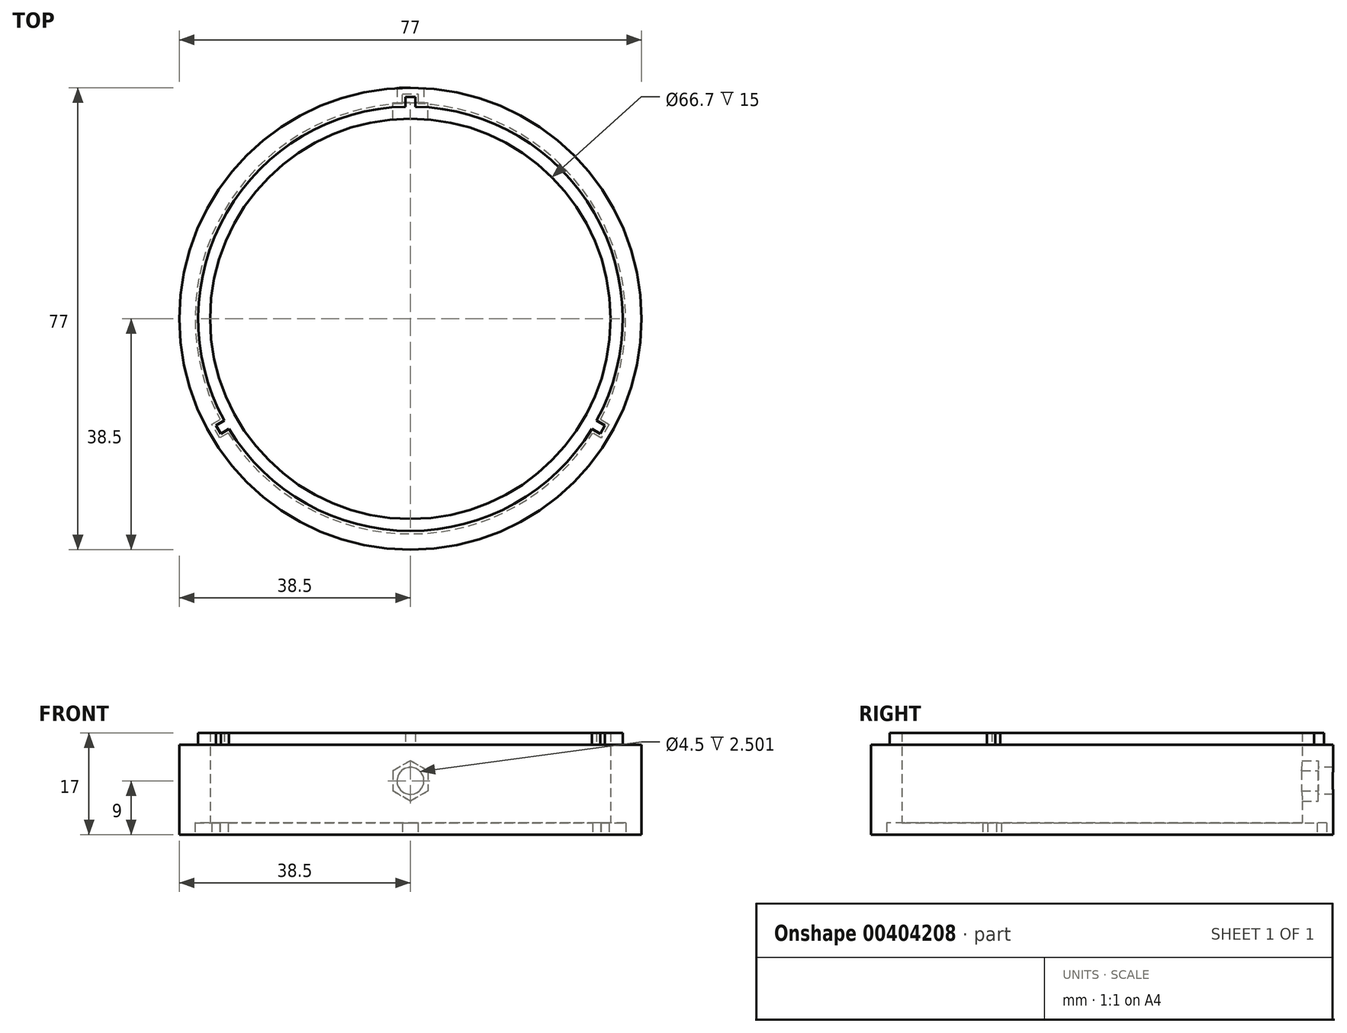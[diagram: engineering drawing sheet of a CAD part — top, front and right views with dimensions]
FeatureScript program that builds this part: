
annotation { "Feature Type Name" : "Feature", "Feature Type Description" : "" }
export const myFeature = defineFeature(function(context is Context, id is Id, definition is map)
    precondition{}
    {
        {
            var Q0;
            Q0=qCreatedBy(makeId("Top.planeOp"),FACE);
            var sketch = newSketch(context, id + "F0", { "sketchPlane" : qUnion([Q0])});
            skCircle(sketch, "E0", {"center": v(0, 0) * mm, "radius": 33.35 * mm});
            skCircle(sketch, "E1", {"center": v(0, 0) * mm, "radius": 38.5 * mm});
            skSolve(sketch);
        }
        {
            var Q0;
            Q0=qSketchRegion(id+"F0",true);
            extrude(context, id + "F1", {"entities" : qUnion([Q0]), "depth" : 15 * mm});
        }
        {
            var Q0;
            Q0=qCreatedBy(makeId("Front.planeOp"),FACE);
            var sketch = newSketch(context, id + "F2", { "sketchPlane" : qUnion([Q0])});
            skCircle(sketch, "E2", {"center": v(0, 9) * mm, "radius": 2.25 * mm});
            skSolve(sketch);
        }
        {
            var Q0;
            Q0=qSketchRegion(id+"F2",true);
            extrude(context, id + "F3", {"entities" : qUnion([Q0]), "operationType" : NewBodyOperationType.REMOVE, "endBound" : BoundingType.THROUGH_ALL, "oppositeDirection" : true, "depth" : 25 * mm});
        }
        {
            var Q0;
            Q0=qCreatedBy(makeId("Front.planeOp"),FACE);
            cPlane(context, id + "F4", {"entities" : qUnion([Q0]), "cplaneType" : CPlaneType.OFFSET, "offset" : 36 * mm, "oppositeDirection" : true, "width" : 150 * mm, "height" : 150 * mm});
        }
        {
            var Q0;
            Q0=qCreatedBy(id+"F4.planeOp",FACE);
            var sketch = newSketch(context, id + "F5", { "sketchPlane" : qUnion([Q0])});
            skCircle(sketch, "E3.cCircle", {"center": v(0, 9) * mm, "radius": 2.92 * mm, "construction": true});
            skLineSegment(sketch, "E3.0", {"start": v(2.92, 10.68) * mm, "end": v(2.92, 7.32) * mm});
            skLineSegment(sketch, "E3.1", {"start": v(2.92, 7.32) * mm, "end": v(0, 5.63) * mm});
            skLineSegment(sketch, "E3.2", {"start": v(0, 5.63) * mm, "end": v(-2.92, 7.32) * mm});
            skLineSegment(sketch, "E3.3", {"start": v(-2.92, 7.32) * mm, "end": v(-2.92, 10.68) * mm});
            skLineSegment(sketch, "E3.4", {"start": v(-2.92, 10.68) * mm, "end": v(0, 12.37) * mm});
            skLineSegment(sketch, "E3.5", {"start": v(0, 12.37) * mm, "end": v(2.92, 10.68) * mm});
            skPoint(sketch, "E3.0.midPoint", {"position": v(2.92, 9) * mm});
            skSolve(sketch);
        }
        {
            var Q0;
            Q0=qSketchRegion(id+"F5",true);
            extrude(context, id + "F6", {"entities" : qUnion([Q0]), "operationType" : NewBodyOperationType.REMOVE, "depth" : 4 * mm});
        }
        {
            var Q0;
            Q0=makeQuery(id+"F1.opExtrude","CAP_FACE",FACE,{"disambiguationData":[OSD([sQuery(id+"F0.wireOp",EDGE,"E0"),sQuery(id+"F0.wireOp",EDGE,"E1")])],"isStart":false});
            var sketch = newSketch(context, id + "F7", { "sketchPlane" : qUnion([Q0])});
            skCircle(sketch, "E4", {"center": v(0, 0) * mm, "radius": 33.35 * mm});
            skArc(sketch, "E5", {"start": v(-0.8, 35.34) * mm, "mid": v(-30.61, 17.68) * mm, "end": v(-31, -16.98) * mm});
            skLineSegment(sketch, "E6", {"start": v(-0.8, 35.34) * mm, "end": v(-0.8, 36.94) * mm});
            skLineSegment(sketch, "E7.MirrorCS", {"start": v(0.8, 35.34) * mm, "end": v(0.8, 36.94) * mm});
            skLineSegment(sketch, "E8", {"start": v(-0.8, 36.94) * mm, "end": v(0.8, 36.94) * mm});
            skLineSegment(sketch, "E9.1.0", {"start": v(-30.2, -18.36) * mm, "end": v(-31.6, -19.16) * mm});
            skLineSegment(sketch, "E9.1.1", {"start": v(-31.6, -19.16) * mm, "end": v(-32.4, -17.78) * mm});
            skLineSegment(sketch, "E9.1.2", {"start": v(-31, -16.98) * mm, "end": v(-32.4, -17.78) * mm});
            skLineSegment(sketch, "E9.2.0", {"start": v(31, -16.98) * mm, "end": v(32.4, -17.78) * mm});
            skLineSegment(sketch, "E9.2.1", {"start": v(32.4, -17.78) * mm, "end": v(31.6, -19.16) * mm});
            skLineSegment(sketch, "E9.2.2", {"start": v(30.2, -18.36) * mm, "end": v(31.6, -19.16) * mm});
            skArc(sketch, "E10.trimOffspring", {"start": v(-30.2, -18.36) * mm, "mid": v(0, -35.35) * mm, "end": v(30.2, -18.36) * mm});
            skArc(sketch, "E11.trimOffspring", {"start": v(31, -16.98) * mm, "mid": v(30.61, 17.67) * mm, "end": v(0.8, 35.34) * mm});
            skSolve(sketch);
        }
        {
            var Q0;
            Q0=qSketchRegion(id+"F7",true);
            extrude(context, id + "F8", {"entities" : qUnion([Q0]), "operationType" : NewBodyOperationType.ADD, "depth" : 2 * mm});
        }
        {
            var Q0;
            Q0=qCreatedBy(makeId("Top.planeOp"),FACE);
            var sketch = newSketch(context, id + "F9", { "sketchPlane" : qUnion([Q0])});
            skArc(sketch, "E12", {"start": v(-1.3, 35.83) * mm, "mid": v(-31.05, 17.93) * mm, "end": v(-31.68, -16.79) * mm});
            skLineSegment(sketch, "E13", {"start": v(-1.3, 35.83) * mm, "end": v(-1.3, 37.44) * mm});
            skLineSegment(sketch, "E14", {"start": v(-1.3, 37.44) * mm, "end": v(1.3, 37.44) * mm});
            skLineSegment(sketch, "E15", {"start": v(1.3, 37.44) * mm, "end": v(1.3, 35.83) * mm});
            skLineSegment(sketch, "E16.1.0", {"start": v(-30.38, -19.04) * mm, "end": v(-31.77, -19.85) * mm});
            skLineSegment(sketch, "E16.1.1", {"start": v(-31.77, -19.85) * mm, "end": v(-33.07, -17.6) * mm});
            skLineSegment(sketch, "E16.1.2", {"start": v(-33.07, -17.6) * mm, "end": v(-31.68, -16.79) * mm});
            skLineSegment(sketch, "E16.2.0", {"start": v(31.68, -16.79) * mm, "end": v(33.07, -17.6) * mm});
            skLineSegment(sketch, "E16.2.1", {"start": v(33.07, -17.6) * mm, "end": v(31.77, -19.85) * mm});
            skLineSegment(sketch, "E16.2.2", {"start": v(31.77, -19.85) * mm, "end": v(30.38, -19.04) * mm});
            skArc(sketch, "E17.trimOffspring", {"start": v(31.68, -16.79) * mm, "mid": v(31.05, 17.92) * mm, "end": v(1.3, 35.83) * mm});
            skArc(sketch, "E18.trimOffspring", {"start": v(-30.38, -19.04) * mm, "mid": v(0, -35.85) * mm, "end": v(30.38, -19.04) * mm});
            skSolve(sketch);
        }
        {
            var Q0;
            Q0 = qSketchRegion(id + "F9", true);
            extrude(context, id + "F10", {"entities" : qUnion([Q0]), "operationType" : NewBodyOperationType.REMOVE, "depth" : 2 * mm});
        }
    });
